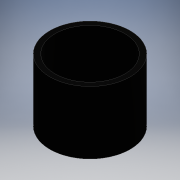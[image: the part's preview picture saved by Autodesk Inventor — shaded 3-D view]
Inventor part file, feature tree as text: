
AUTODESK INVENTOR PART (.ipt)
format: ipt  version: 2016 (Build 200138000, 138)  size: 90,624 bytes
history: native  units: mm
features: other x1, sketch x1, extrude x1
ambient origin geometry x8: Origin, YZ Plane, XZ Plane, XY Plane, X Axis, Y Axis, Z Axis, Center Point
bodies: Body1 (feature_tree)
feature tree (3):
  other  "ソリッド1"
  sketch  "スケッチ1"
  extrude  "押し出し1"  Depth=20.0mm
